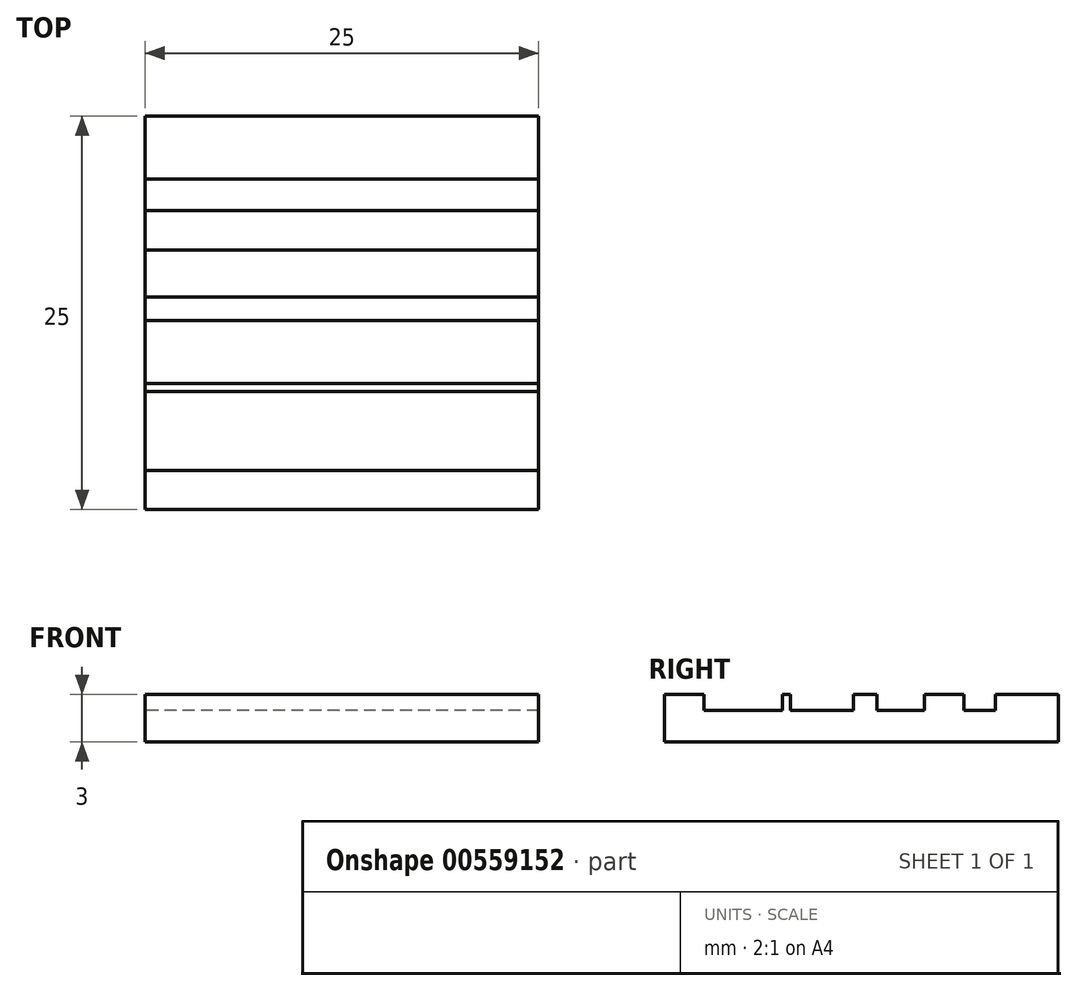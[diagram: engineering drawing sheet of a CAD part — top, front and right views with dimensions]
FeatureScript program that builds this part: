
annotation { "Feature Type Name" : "Feature", "Feature Type Description" : "" }
export const myFeature = defineFeature(function(context is Context, id is Id, definition is map)
    precondition{}
    {
        {
            var Q0;
            Q0=qCreatedBy(makeId("Top.planeOp"),FACE);
            var sketch = newSketch(context, id + "F0", { "sketchPlane" : qUnion([Q0])});
            skLineSegment(sketch, "E0.bottom", {"start": v(12.5, 12.5) * mm, "end": v(-12.5, 12.5) * mm});
            skLineSegment(sketch, "E0.top", {"start": v(12.5, -12.5) * mm, "end": v(-12.5, -12.5) * mm});
            skLineSegment(sketch, "E0.left", {"start": v(12.5, 12.5) * mm, "end": v(12.5, -12.5) * mm});
            skLineSegment(sketch, "E0.right", {"start": v(-12.5, 12.5) * mm, "end": v(-12.5, -12.5) * mm});
            skPoint(sketch, "E0.middle", {"position": v(0, 0) * mm});
            skSolve(sketch);
        }
        {
            var Q0;
            Q0 = qSketchRegion(id + "F0", true);
            extrude(context, id + "F1", {"entities" : qUnion([Q0]), "depth" : 3 * mm, "offsetDistance" : 25 * mm});
        }
        {
            var Q0;
            Q0=makeQuery(id+"F1.opExtrude","CAP_FACE",FACE,{"disambiguationData":[OSD([sQuery(id+"F0.wireOp",EDGE,"E0.bottom"),sQuery(id+"F0.wireOp",EDGE,"E0.top"),sQuery(id+"F0.wireOp",EDGE,"E0.left"),sQuery(id+"F0.wireOp",EDGE,"E0.right")])],"isStart":false});
            var sketch = newSketch(context, id + "F2", { "sketchPlane" : qUnion([Q0])});
            skLineSegment(sketch, "E1.bottom", {"start": v(13, 8.5) * mm, "end": v(-13, 8.5) * mm});
            skLineSegment(sketch, "E1.top", {"start": v(13, 6.5) * mm, "end": v(-13, 6.5) * mm});
            skLineSegment(sketch, "E1.left", {"start": v(13, 8.5) * mm, "end": v(13, 6.5) * mm});
            skLineSegment(sketch, "E1.right", {"start": v(-13, 8.5) * mm, "end": v(-13, 6.5) * mm});
            skPoint(sketch, "E1.middle", {"position": v(0, 7.5) * mm});
            skLineSegment(sketch, "E2.bottom", {"start": v(13, 4) * mm, "end": v(-13, 4) * mm});
            skLineSegment(sketch, "E2.top", {"start": v(13, 1) * mm, "end": v(-13, 1) * mm});
            skLineSegment(sketch, "E2.left", {"start": v(13, 4) * mm, "end": v(13, 1) * mm});
            skLineSegment(sketch, "E2.right", {"start": v(-13, 4) * mm, "end": v(-13, 1) * mm});
            skPoint(sketch, "E2.middle", {"position": v(0, 2.5) * mm});
            skLineSegment(sketch, "E3.bottom", {"start": v(13, -0.5) * mm, "end": v(-13, -0.5) * mm});
            skLineSegment(sketch, "E3.top", {"start": v(13, -4.5) * mm, "end": v(-13, -4.5) * mm});
            skLineSegment(sketch, "E3.left", {"start": v(13, -0.5) * mm, "end": v(13, -4.5) * mm});
            skLineSegment(sketch, "E3.right", {"start": v(-13, -0.5) * mm, "end": v(-13, -4.5) * mm});
            skPoint(sketch, "E3.middle", {"position": v(0, -2.5) * mm});
            skLineSegment(sketch, "E4.bottom", {"start": v(13, -5) * mm, "end": v(-13, -5) * mm});
            skLineSegment(sketch, "E4.top", {"start": v(13, -10) * mm, "end": v(-13, -10) * mm});
            skLineSegment(sketch, "E4.left", {"start": v(13, -5) * mm, "end": v(13, -10) * mm});
            skLineSegment(sketch, "E4.right", {"start": v(-13, -5) * mm, "end": v(-13, -10) * mm});
            skPoint(sketch, "E4.middle", {"position": v(0, -7.5) * mm});
            skSolve(sketch);
        }
        {
            var Q0;
            {var subQ0=sQuery(id+"F2.wireOp",EDGE,"E1.bottom");var subQ1=makeQuery(id+"F1.opExtrude","CAP_EDGE",EDGE,{"disambiguationData":[OSD([sQuery(id+"F0.wireOp",EDGE,"E0.left")])],"isStart":false});var subQ2=makeQuery(id+"F2.imprint","INTERSECT",VERTEX,{"derivedFrom":[subQ1,subQ0]});Q0=makeQuery(id+"F2.imprint","IMPRINT",FACE,{"disambiguationData":[TD([[makeQuery(id+"F2.imprint","IMPRINT",EDGE,{"disambiguationData":[TD([[subQ2,-1.0]])],"derivedFrom":subQ0}),1.0]])]});}
            var Q1;
            {var subQ0=sQuery(id+"F2.wireOp",EDGE,"E2.bottom");var subQ1=makeQuery(id+"F1.opExtrude","CAP_EDGE",EDGE,{"disambiguationData":[OSD([sQuery(id+"F0.wireOp",EDGE,"E0.left")])],"isStart":false});var subQ2=makeQuery(id+"F2.imprint","INTERSECT",VERTEX,{"derivedFrom":[subQ1,subQ0]});Q1=makeQuery(id+"F2.imprint","IMPRINT",FACE,{"disambiguationData":[TD([[makeQuery(id+"F2.imprint","IMPRINT",EDGE,{"disambiguationData":[TD([[subQ2,-1.0]])],"derivedFrom":subQ0}),1.0]])]});}
            var Q2;
            {var subQ0=sQuery(id+"F2.wireOp",EDGE,"E3.bottom");var subQ1=makeQuery(id+"F1.opExtrude","CAP_EDGE",EDGE,{"disambiguationData":[OSD([sQuery(id+"F0.wireOp",EDGE,"E0.left")])],"isStart":false});var subQ2=makeQuery(id+"F2.imprint","INTERSECT",VERTEX,{"derivedFrom":[subQ1,subQ0]});Q2=makeQuery(id+"F2.imprint","IMPRINT",FACE,{"disambiguationData":[TD([[makeQuery(id+"F2.imprint","IMPRINT",EDGE,{"disambiguationData":[TD([[subQ2,-1.0]])],"derivedFrom":subQ0}),1.0]])]});}
            var Q3;
            {var subQ0=sQuery(id+"F2.wireOp",EDGE,"E4.bottom");var subQ1=makeQuery(id+"F1.opExtrude","CAP_EDGE",EDGE,{"disambiguationData":[OSD([sQuery(id+"F0.wireOp",EDGE,"E0.left")])],"isStart":false});var subQ2=makeQuery(id+"F2.imprint","INTERSECT",VERTEX,{"derivedFrom":[subQ1,subQ0]});Q3=makeQuery(id+"F2.imprint","IMPRINT",FACE,{"disambiguationData":[TD([[makeQuery(id+"F2.imprint","IMPRINT",EDGE,{"disambiguationData":[TD([[subQ2,-1.0]])],"derivedFrom":subQ0}),1.0]])]});}
            extrude(context, id + "F3", {"entities" : qUnion([Q0, Q1, Q2, Q3]), "depth" : -1 * mm, "offsetDistance" : 25 * mm});
        }
        {
            var Q0;
            Q0=makeQuery(id+"F3.opExtrude","SWEPT_BODY",BODY,{"disambiguationData":[OSD([sQuery(id+"F0.wireOp",EDGE,"E0.left"),sQuery(id+"F0.wireOp",EDGE,"E0.right"),sQuery(id+"F2.wireOp",EDGE,"E1.bottom"),sQuery(id+"F2.wireOp",EDGE,"E1.top")])]});
            var Q1;
            Q1=makeQuery(id+"F3.opExtrude","SWEPT_BODY",BODY,{"disambiguationData":[OSD([sQuery(id+"F0.wireOp",EDGE,"E0.left"),sQuery(id+"F0.wireOp",EDGE,"E0.right"),sQuery(id+"F2.wireOp",EDGE,"E2.bottom"),sQuery(id+"F2.wireOp",EDGE,"E2.top")])]});
            var Q2;
            Q2=makeQuery(id+"F3.opExtrude","SWEPT_BODY",BODY,{"disambiguationData":[OSD([sQuery(id+"F0.wireOp",EDGE,"E0.left"),sQuery(id+"F0.wireOp",EDGE,"E0.right"),sQuery(id+"F2.wireOp",EDGE,"E3.bottom"),sQuery(id+"F2.wireOp",EDGE,"E3.top")])]});
            var Q3;
            Q3=makeQuery(id+"F3.opExtrude","SWEPT_BODY",BODY,{"disambiguationData":[OSD([sQuery(id+"F0.wireOp",EDGE,"E0.left"),sQuery(id+"F0.wireOp",EDGE,"E0.right"),sQuery(id+"F2.wireOp",EDGE,"E4.bottom"),sQuery(id+"F2.wireOp",EDGE,"E4.top")])]});
            var Q4;
            Q4=makeQuery(id+"F1.opExtrude","SWEPT_BODY",BODY,{"disambiguationData":[OSD([sQuery(id+"F0.wireOp",EDGE,"E0.bottom"),sQuery(id+"F0.wireOp",EDGE,"E0.top"),sQuery(id+"F0.wireOp",EDGE,"E0.left"),sQuery(id+"F0.wireOp",EDGE,"E0.right")])]});
            booleanBodies(context, id + "F4", {"operationType" : BooleanOperationType.SUBTRACTION, "tools" : qUnion([Q0, Q1, Q2, Q3]), "targets" : qUnion([Q4])});
        }
    });
